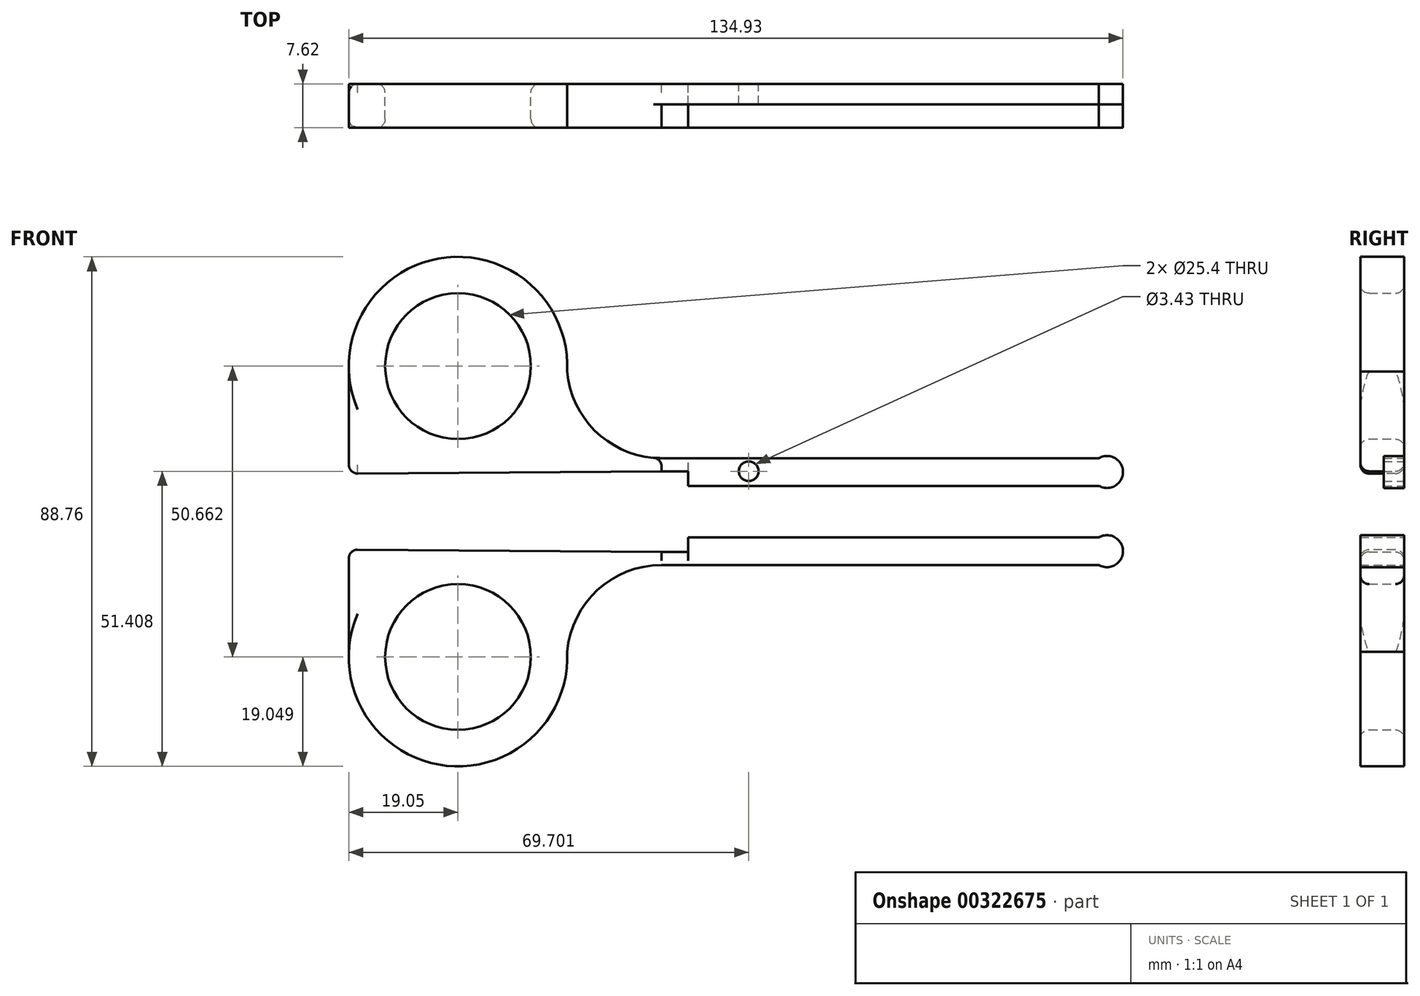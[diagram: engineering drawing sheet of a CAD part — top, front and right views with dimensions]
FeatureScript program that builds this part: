
annotation { "Feature Type Name" : "Feature", "Feature Type Description" : "" }
export const myFeature = defineFeature(function(context is Context, id is Id, definition is map)
    precondition{}
    {
        {
            var Q0;
            Q0=qCreatedBy(makeId("Front.planeOp"),FACE);
            var sketch = newSketch(context, id + "F0", { "sketchPlane" : qUnion([Q0])});
            skLineSegment(sketch, "E0", {"start": v(-11.08, 9.31) * mm, "end": v(65.12, 9.31) * mm});
            skLineSegment(sketch, "E1", {"start": v(-6.45, 4.49) * mm, "end": v(65.12, 4.49) * mm});
            skArc(sketch, "E2", {"start": v(65.12, 4.49) * mm, "mid": v(69.32, 6.9) * mm, "end": v(65.12, 9.31) * mm});
            skLineSegment(sketch, "E3", {"start": v(-11.08, 9.31) * mm, "end": v(-11.08, 7.03) * mm});
            skLineSegment(sketch, "E4", {"start": v(-11.08, 7.03) * mm, "end": v(-6.45, 7.03) * mm});
            skLineSegment(sketch, "E5", {"start": v(-6.45, 7.03) * mm, "end": v(-6.45, 4.49) * mm});
            skLineSegment(sketch, "E6", {"start": v(-65.59, 6.62) * mm, "end": v(-65.59, 24.4) * mm});
            skArc(sketch, "E7", {"start": v(-27.53, 24.4) * mm, "mid": v(-46.56, 44.38) * mm, "end": v(-65.59, 24.4) * mm});
            skCircle(sketch, "E8", {"center": v(-46.56, 25.33) * mm, "radius": 12.7 * mm});
            skCircle(sketch, "E9", {"center": v(4.1, 7.03) * mm, "radius": 1.71 * mm});
            skLineSegment(sketch, "E10", {"start": v(-65.59, 6.62) * mm, "end": v(-11.08, 7.03) * mm});
            skArc(sketch, "E11", {"start": v(-27.53, 24.4) * mm, "mid": v(-22.24, 13.66) * mm, "end": v(-11.08, 9.31) * mm});
            skLineSegment(sketch, "E12", {"start": v(-6.45, 0) * mm, "end": v(65.12, 0) * mm});
            skLineSegment(sketch, "E13.MirrorCS", {"start": v(-11.08, -9.31) * mm, "end": v(65.12, -9.31) * mm});
            skLineSegment(sketch, "E14.MirrorCS", {"start": v(-6.45, -4.49) * mm, "end": v(65.12, -4.49) * mm});
            skArc(sketch, "E15.MirrorCS", {"start": v(65.12, -4.49) * mm, "mid": v(69.32, -6.9) * mm, "end": v(65.12, -9.31) * mm});
            skLineSegment(sketch, "E16.MirrorCS", {"start": v(-6.45, -7.03) * mm, "end": v(-6.45, -4.49) * mm});
            skLineSegment(sketch, "E17.MirrorCS", {"start": v(-11.08, -7.03) * mm, "end": v(-6.45, -7.03) * mm});
            skLineSegment(sketch, "E18.MirrorCS", {"start": v(-65.59, -6.62) * mm, "end": v(-11.08, -7.03) * mm});
            skArc(sketch, "E19.MirrorCS", {"start": v(-27.53, -24.4) * mm, "mid": v(-22.24, -13.66) * mm, "end": v(-11.08, -9.31) * mm});
            skArc(sketch, "E20.MirrorCS", {"start": v(-27.53, -24.4) * mm, "mid": v(-46.56, -44.38) * mm, "end": v(-65.59, -24.4) * mm});
            skCircle(sketch, "E21.MirrorC", {"center": v(-46.56, -25.33) * mm, "radius": 12.7 * mm});
            skLineSegment(sketch, "E22.MirrorCS", {"start": v(-65.59, -6.62) * mm, "end": v(-65.59, -24.4) * mm});
            skSolve(sketch);
        }
        {
            var Q0;
            Q0=makeQuery(id+"F0.imprint","IMPRINT",FACE,{"disambiguationData":[TD([[makeQuery(id+"F0.imprint","IMPRINT",EDGE,{"derivedFrom":sQuery(id+"F0.wireOp",EDGE,"E3")}),-1.0]])]});
            extrude(context, id + "F1", {"entities" : qUnion([Q0]), "depth" : 7.62 * mm});
        }
        {
            var Q0;
            Q0=makeQuery(id+"F0.imprint","IMPRINT",FACE,{"disambiguationData":[TD([[makeQuery(id+"F0.imprint","IMPRINT",EDGE,{"derivedFrom":sQuery(id+"F0.wireOp",EDGE,"E0")}),-1.0]])]});
            extrude(context, id + "F2", {"entities" : qUnion([Q0]), "operationType" : NewBodyOperationType.ADD, "depth" : 3.56 * mm});
        }
        {
            var Q0;
            Q0=makeQuery(id+"F1.opExtrude","SWEPT_EDGE",EDGE,{"disambiguationData":[OSD([sQuery(id+"F0.wireOp",EDGE,"E6"),sQuery(id+"F0.wireOp",EDGE,"E10")])]});
            fillet(context, id + "F3", {"entities" : qUnion([Q0]), "radius" : 1.52 * mm, "tangentPropagation" : true, "allowEdgeOverflow" : false});
        }
        {
            var Q0;
            Q0=makeQuery(id+"F1.opExtrude","CAP_EDGE",EDGE,{"disambiguationData":[OSD([sQuery(id+"F0.wireOp",EDGE,"E8")])],"isStart":false});
            fillet(context, id + "F4", {"entities" : qUnion([Q0]), "radius" : 1.52 * mm, "tangentPropagation" : true, "allowEdgeOverflow" : false});
        }
        {
            var Q0;
            Q0=makeQuery(id+"F1.opExtrude","CAP_EDGE",EDGE,{"disambiguationData":[OSD([sQuery(id+"F0.wireOp",EDGE,"E8")])],"isStart":true});
            fillet(context, id + "F5", {"entities" : qUnion([Q0]), "radius" : 1.52 * mm, "tangentPropagation" : true, "allowEdgeOverflow" : false});
        }
        {
            var Q0;
            Q0=makeQuery(id+"F1.opExtrude","CAP_EDGE",EDGE,{"disambiguationData":[OSD([sQuery(id+"F0.wireOp",EDGE,"E10")])],"isStart":true});
            fillet(context, id + "F6", {"entities" : qUnion([Q0]), "radius" : 1.52 * mm, "tangentPropagation" : true, "allowEdgeOverflow" : false});
        }
        {
            var Q0;
            Q0=makeQuery(id+"F1.opExtrude","CAP_EDGE",EDGE,{"disambiguationData":[OSD([sQuery(id+"F0.wireOp",EDGE,"E10")])],"isStart":false});
            fillet(context, id + "F7", {"entities" : qUnion([Q0]), "radius" : 1.52 * mm, "tangentPropagation" : true, "allowEdgeOverflow" : false});
        }
        {
            var Q0;
            Q0=makeQuery(id+"F2.boolean.opBoolean","SPLIT",EDGE,{"derivedFrom":makeQuery(id+"F1.opExtrude","SWEPT_EDGE",EDGE,{"disambiguationData":[OSD([sQuery(id+"F0.wireOp",EDGE,"E0"),sQuery(id+"F0.wireOp",EDGE,"E3"),sQuery(id+"F0.wireOp",EDGE,"E11")])]})});
            fillet(context, id + "F8", {"entities" : qUnion([Q0]), "radius" : 1.52 * mm, "tangentPropagation" : true, "allowEdgeOverflow" : false});
        }
        {
            var Q0;
            Q0=makeQuery(id+"F0.imprint","IMPRINT",FACE,{"disambiguationData":[TD([[makeQuery(id+"F0.imprint","IMPRINT",EDGE,{"derivedFrom":sQuery(id+"F0.wireOp",EDGE,"E13.MirrorCS")}),1.0]])]});
            extrude(context, id + "F9", {"entities" : qUnion([Q0]), "depth" : 7.62 * mm});
        }
        {
            var Q0;
            Q0=makeQuery(id+"F9.opExtrude","CAP_EDGE",EDGE,{"disambiguationData":[OSD([sQuery(id+"F0.wireOp",EDGE,"E21.MirrorC")])],"isStart":false});
            fillet(context, id + "F10", {"entities" : qUnion([Q0]), "radius" : 1.52 * mm, "tangentPropagation" : true, "allowEdgeOverflow" : false});
        }
        {
            var Q0;
            Q0=makeQuery(id+"F9.opExtrude","CAP_EDGE",EDGE,{"disambiguationData":[OSD([sQuery(id+"F0.wireOp",EDGE,"E21.MirrorC")])],"isStart":true});
            fillet(context, id + "F11", {"entities" : qUnion([Q0]), "radius" : 1.52 * mm, "tangentPropagation" : true, "allowEdgeOverflow" : false});
        }
        {
            var Q0;
            Q0=makeQuery(id+"F9.opExtrude","SWEPT_EDGE",EDGE,{"disambiguationData":[OSD([sQuery(id+"F0.wireOp",EDGE,"E18.MirrorCS"),sQuery(id+"F0.wireOp",EDGE,"E22.MirrorCS")])]});
            fillet(context, id + "F12", {"entities" : qUnion([Q0]), "radius" : 1.52 * mm, "tangentPropagation" : true, "allowEdgeOverflow" : false});
        }
        {
            var Q0;
            Q0=makeQuery(id+"F9.opExtrude","CAP_EDGE",EDGE,{"disambiguationData":[OSD([sQuery(id+"F0.wireOp",EDGE,"E22.MirrorCS")])],"isStart":true});
            fillet(context, id + "F13", {"entities" : qUnion([Q0]), "radius" : 1.52 * mm, "tangentPropagation" : true, "allowEdgeOverflow" : false});
        }
        {
            var Q0;
            Q0=makeQuery(id+"F9.opExtrude","CAP_EDGE",EDGE,{"disambiguationData":[OSD([sQuery(id+"F0.wireOp",EDGE,"E22.MirrorCS")])],"isStart":false});
            fillet(context, id + "F14", {"entities" : qUnion([Q0]), "radius" : 1.52 * mm, "tangentPropagation" : true, "allowEdgeOverflow" : false});
        }
    });
